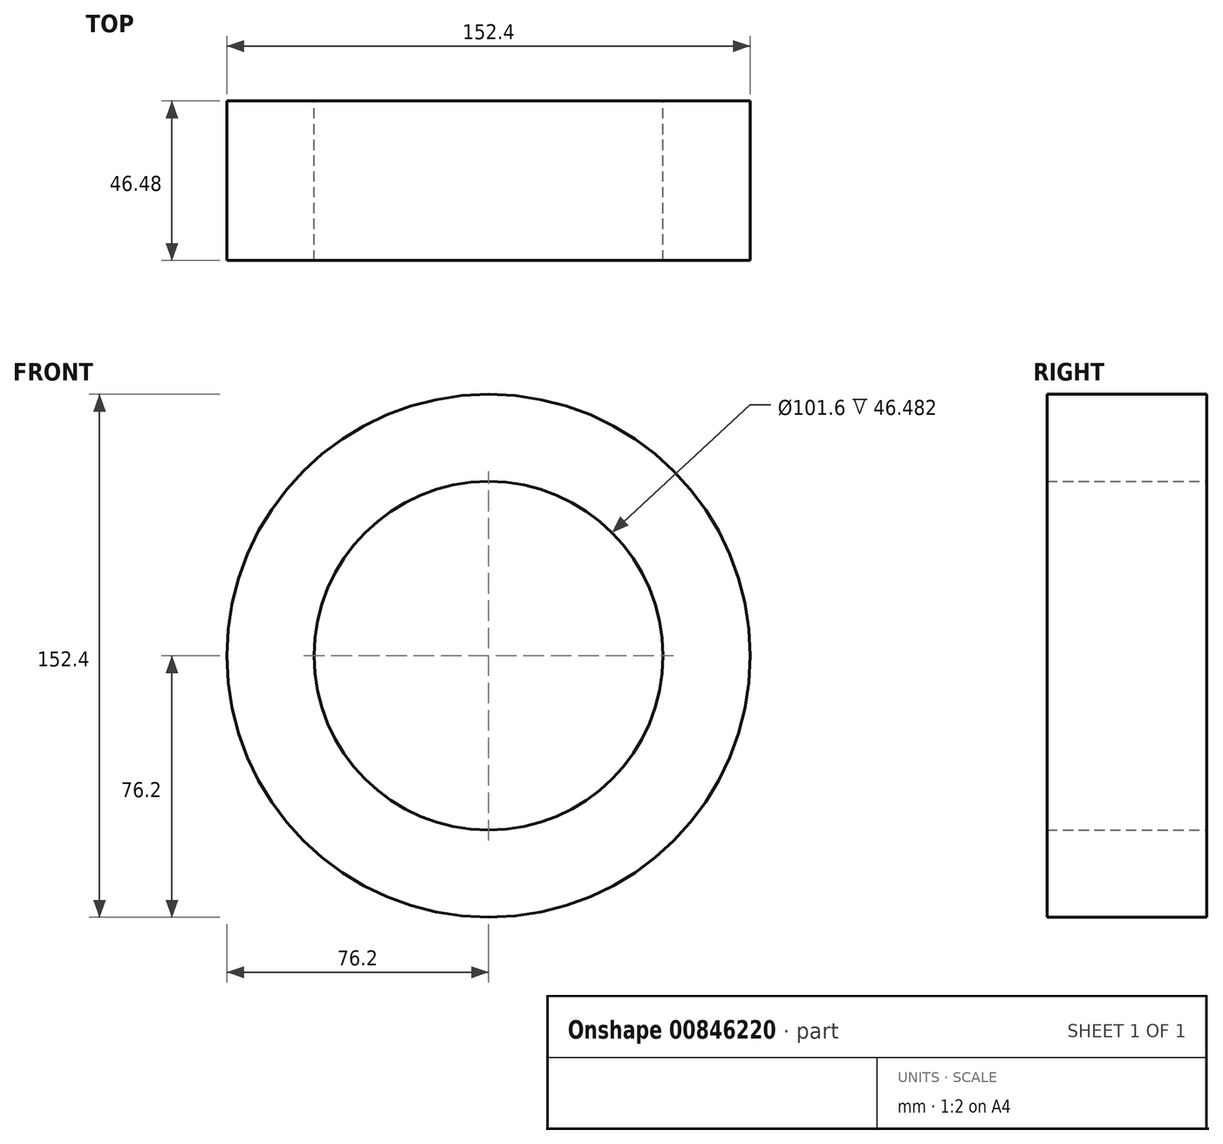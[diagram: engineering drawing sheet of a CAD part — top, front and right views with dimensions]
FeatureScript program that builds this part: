
annotation { "Feature Type Name" : "Feature", "Feature Type Description" : "" }
export const myFeature = defineFeature(function(context is Context, id is Id, definition is map)
    precondition{}
    {
        {
            var Q0;
            Q0=qCreatedBy(makeId("Front.planeOp"),FACE);
            var sketch = newSketch(context, id + "F0", { "sketchPlane" : qUnion([Q0])});
            skCircle(sketch, "E0", {"center": v(0, 0) * mm, "radius": 76.2 * mm});
            skCircle(sketch, "E1", {"center": v(0, 0) * mm, "radius": 50.8 * mm});
            skSolve(sketch);
        }
        {
            var Q0;
            Q0=makeQuery(id+"F0.imprint","IMPRINT",FACE,{"disambiguationData":[TD([[makeQuery(id+"F0.imprint","IMPRINT",EDGE,{"derivedFrom":sQuery(id+"F0.wireOp",EDGE,"E0")}),1.0]])]});
            extrude(context, id + "F1", {"entities" : qUnion([Q0]), "depth" : 46.48 * mm, "offsetDistance" : 25.4 * mm});
        }
    });
